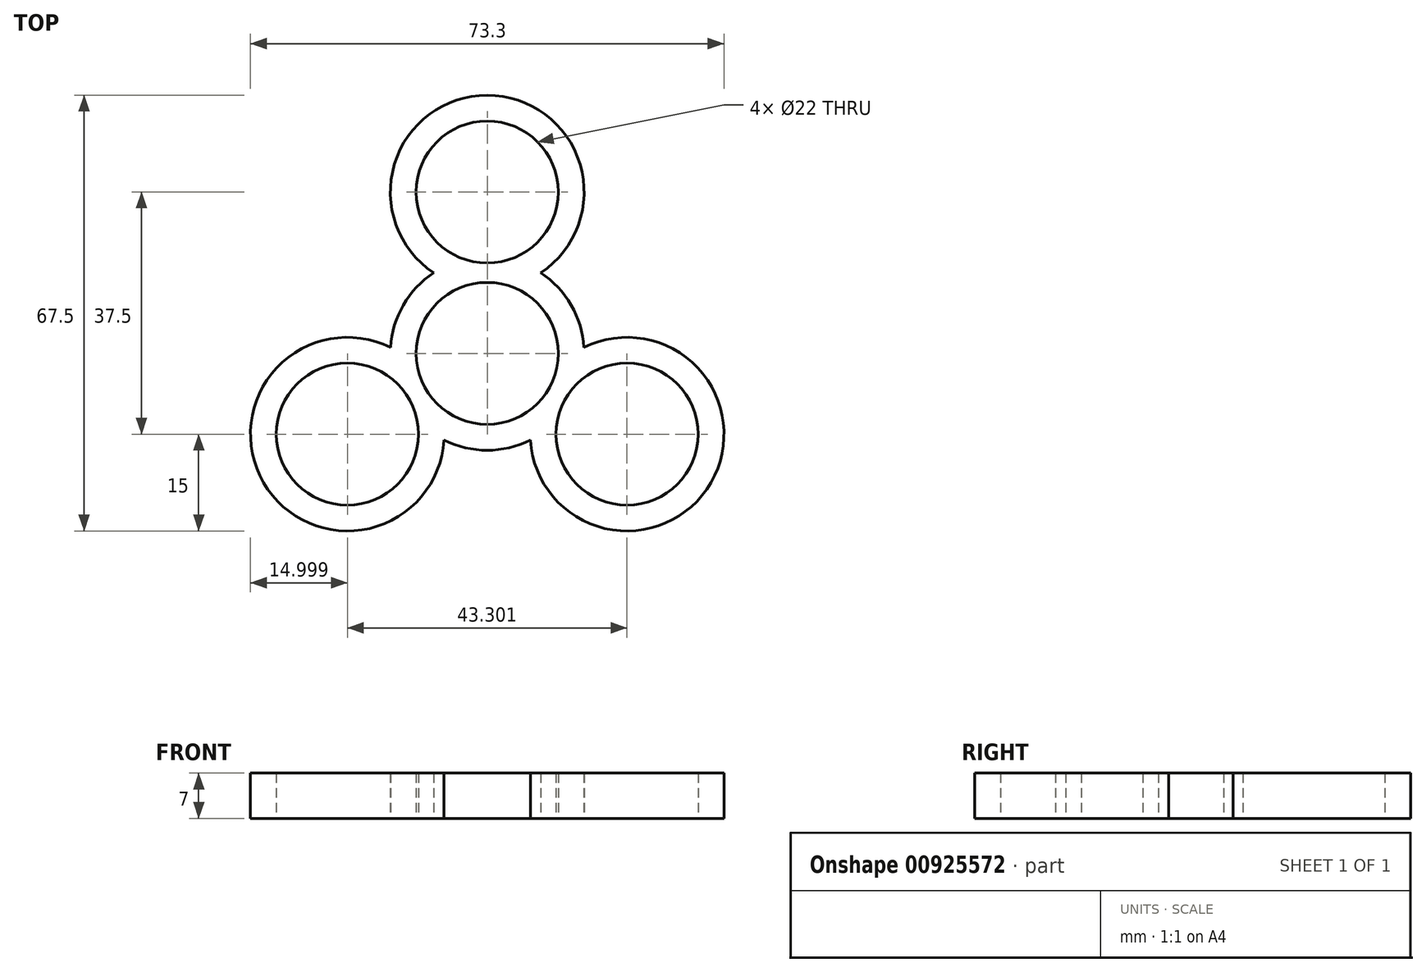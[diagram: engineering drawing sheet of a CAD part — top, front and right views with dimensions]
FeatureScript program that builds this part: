
annotation { "Feature Type Name" : "Feature", "Feature Type Description" : "" }
export const myFeature = defineFeature(function(context is Context, id is Id, definition is map)
    precondition{}
    {
        {
            var Q0;
            Q0=qCreatedBy(makeId("Top.planeOp"),FACE);
            var sketch = newSketch(context, id + "F0", { "sketchPlane" : qUnion([Q0])});
            skArc(sketch, "E0", {"start": v(9.53, 5.5) * mm, "mid": v(0, 11) * mm, "end": v(-9.53, 5.5) * mm});
            skLineSegment(sketch, "E1", {"start": v(0, 10) * mm, "end": v(0, 11) * mm});
            skCircle(sketch, "E2", {"center": v(0, 25) * mm, "radius": 11 * mm});
            skArc(sketch, "E3", {"start": v(-8.3, 12.5) * mm, "mid": v(-10.93, 10.27) * mm, "end": v(-13, 7.5) * mm});
            skArc(sketch, "E4", {"start": v(8.3, 12.5) * mm, "mid": v(0, 40) * mm, "end": v(-8.3, 12.5) * mm});
            skArc(sketch, "E5.trimOffspring", {"start": v(13, 7.5) * mm, "mid": v(10.93, 10.27) * mm, "end": v(8.3, 12.5) * mm});
            skLineSegment(sketch, "E6.trimOffspring", {"start": v(0, 14) * mm, "end": v(0, 15) * mm});
            skCircle(sketch, "E7.1.0", {"center": v(-21.65, -12.5) * mm, "radius": 11 * mm});
            skArc(sketch, "E7.1.1", {"start": v(-14.97, 0.93) * mm, "mid": v(-34.64, -20) * mm, "end": v(-6.68, -13.43) * mm});
            skArc(sketch, "E7.1.2", {"start": v(-6.68, -13.43) * mm, "mid": v(-3.43, -14.6) * mm, "end": v(0, -15) * mm});
            skArc(sketch, "E7.1.3", {"start": v(-9.53, 5.5) * mm, "mid": v(-9.53, -5.5) * mm, "end": v(0, -11) * mm});
            skArc(sketch, "E7.1.4", {"start": v(-13, 7.5) * mm, "mid": v(-14.36, 4.33) * mm, "end": v(-14.97, 0.93) * mm});
            skCircle(sketch, "E7.2.0", {"center": v(21.65, -12.5) * mm, "radius": 11 * mm});
            skArc(sketch, "E7.2.1", {"start": v(6.68, -13.43) * mm, "mid": v(34.64, -20) * mm, "end": v(14.97, 0.93) * mm});
            skArc(sketch, "E7.2.2", {"start": v(14.97, 0.93) * mm, "mid": v(14.36, 4.33) * mm, "end": v(13, 7.5) * mm});
            skArc(sketch, "E7.2.3", {"start": v(0, -11) * mm, "mid": v(9.53, -5.5) * mm, "end": v(9.53, 5.5) * mm});
            skArc(sketch, "E7.2.4", {"start": v(0, -15) * mm, "mid": v(3.43, -14.6) * mm, "end": v(6.68, -13.43) * mm});
            skSolve(sketch);
        }
        {
            var Q0;
            Q0 = qSketchRegion(id + "F0", true);
            extrude(context, id + "F1", {"entities" : qUnion([Q0]), "depth" : 7 * mm, "offsetDistance" : 25 * mm});
        }
    });
